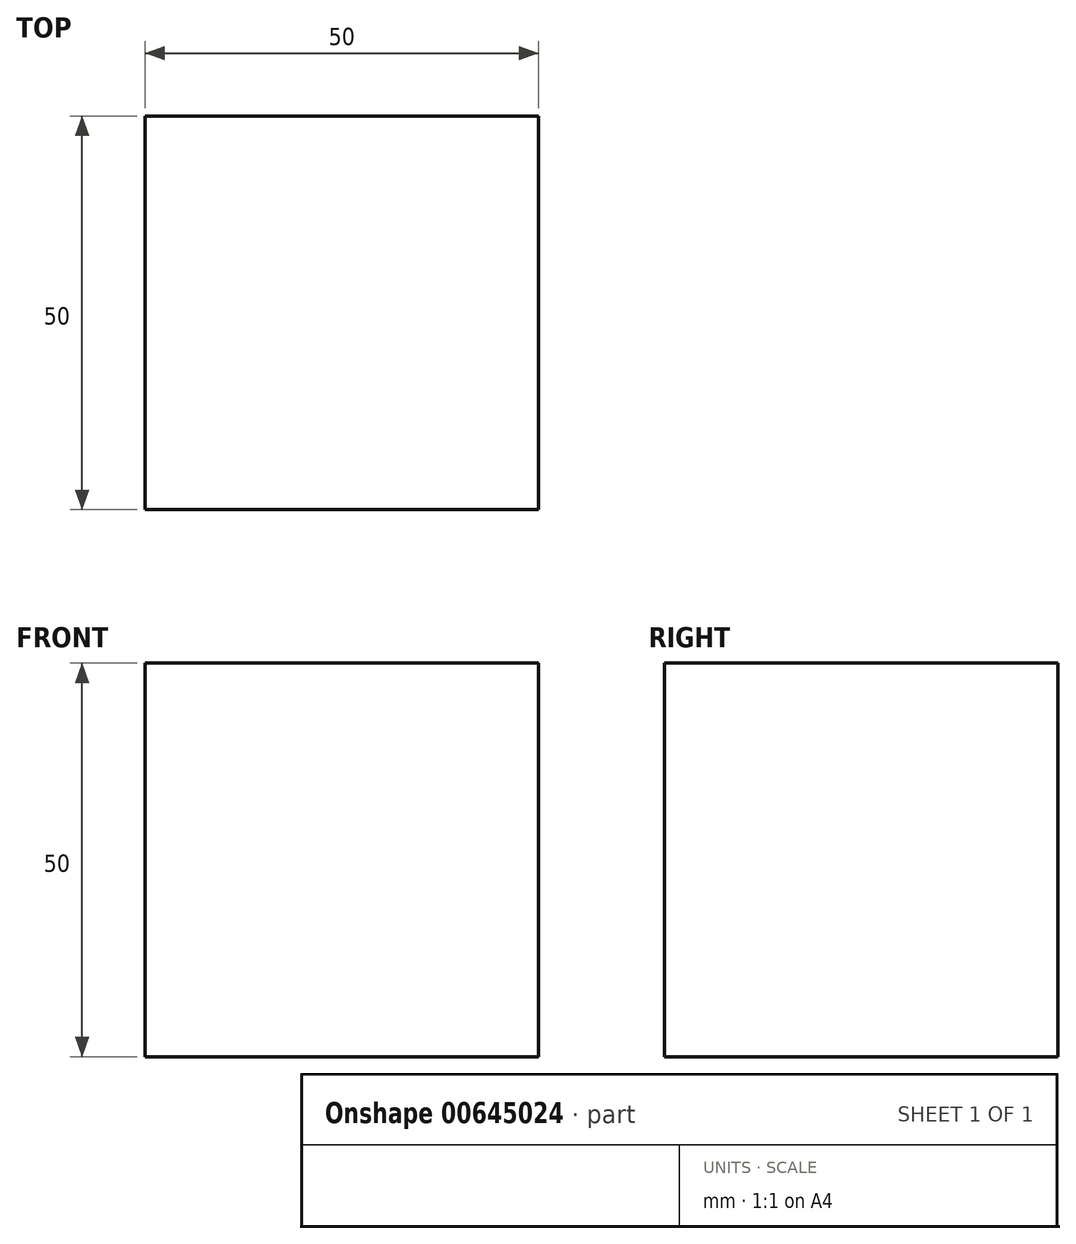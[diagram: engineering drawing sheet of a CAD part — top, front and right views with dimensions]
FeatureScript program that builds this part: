
annotation { "Feature Type Name" : "Feature", "Feature Type Description" : "" }
export const myFeature = defineFeature(function(context is Context, id is Id, definition is map)
    precondition{}
    {
        {
            var Q0;
            Q0=qCreatedBy(makeId("Top.planeOp"),FACE);
            var sketch = newSketch(context, id + "F0", { "sketchPlane" : qUnion([Q0])});
            skLineSegment(sketch, "E0.bottom", {"start": v(-16.48, 17.84) * mm, "end": v(-66.48, 17.84) * mm});
            skLineSegment(sketch, "E0.top", {"start": v(-16.48, -32.16) * mm, "end": v(-66.48, -32.16) * mm});
            skLineSegment(sketch, "E0.left", {"start": v(-16.48, 17.84) * mm, "end": v(-16.48, -32.16) * mm});
            skLineSegment(sketch, "E0.right", {"start": v(-66.48, 17.84) * mm, "end": v(-66.48, -32.16) * mm});
            skSolve(sketch);
        }
        {
            var Q0;
            Q0 = qSketchRegion(id + "F0", true);
            extrude(context, id + "F1", {"entities" : qUnion([Q0]), "depth" : 50 * mm, "offsetDistance" : 25 * mm});
        }
    });
